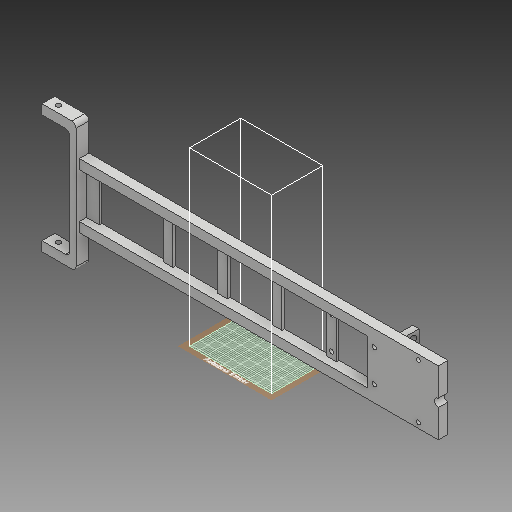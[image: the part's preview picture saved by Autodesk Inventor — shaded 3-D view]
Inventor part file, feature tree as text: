
AUTODESK INVENTOR PART (.ipt)
format: ipt  version: 2018 (Build 220112000, 112)  size: 794,624 bytes
history: native  units: mm
features: sketch x47, extrude x36, fillet x8, hole x6, plane x1
ambient origin geometry x8: Origin, YZ Plane, XZ Plane, XY Plane, X Axis, Y Axis, Z Axis, Center Point
bodies: Solid1 (feature_tree)
feature tree (98):
  extrude  "Extrusion1"  Depth=50.0mm
  hole  "Hole1"  [1 undecoded]
  hole  "Hole2"  [1 undecoded]
  extrude  "Extrusion2"  Depth=25.0mm
  extrude  "Extrusion3"  Depth=25.0mm
  extrude  "Extrusion4"  Depth=5.0mm
  sketch  "Sketch7"  dims[d25=10.0mm d26=5.0mm]
  extrude  "Extrusion5"  Depth=5.0mm
  extrude  "Extrusion6"  Depth=35.0mm
  extrude  "Extrusion7"  Depth=35.0mm
  extrude  "Extrusion8"  Depth=35.0mm
  extrude  "Extrusion9"  Depth=2.0mm TaperAngle=0.0deg
  extrude  "Extrusion10"  Depth=7.5mm TaperAngle=0.0deg
  extrude  "Extrusion11"  Depth=10.0mm
  extrude  "Extrusion12"  Depth=7.5mm
  fillet  "Fillet1"  Radius=7.5mm
  fillet  "Fillet2"  Radius=25.0mm
  fillet  "Fillet3"  Radius=3.0mm
  fillet  "Fillet4"  Radius=3.2mm
  fillet  "Fillet5"  Radius=2.1mm
  fillet  "Fillet6"  Radius=5.5mm
  extrude  "Extrusion13"  Depth=92.5mm TaperAngle=0.0deg
  sketch  "Sketch17"  dims[d58=4.25mm d59=241.0mm d60=0.0mm]
  hole  "Hole3"  [1 undecoded]
  hole  "Hole4"  [1 undecoded]
  extrude  "Extrusion14"  Depth=5.0mm
  extrude  "Extrusion15"  Depth=2.5mm TaperAngle=0.0deg
  extrude  "Extrusion16"  Depth=6.35mm
  extrude  "Extrusion17"  Depth=2.5mm
  extrude  "Extrusion18"  Depth=14.55mm TaperAngle=0.0deg
  extrude  "Extrusion19"  Depth=0.1mm
  extrude  "Extrusion20"  Depth=3.25mm
  extrude  "Extrusion21"  Depth=3.25mm
  hole  "Hole5"  [1 undecoded]
  extrude  "Extrusion22"  Depth=2.0mm
  extrude  "Extrusion23"  Depth=15.0mm
  extrude  "Extrusion24"  Depth=10.0mm TaperAngle=0.0deg
  hole  "Hole6"  [1 undecoded]
  extrude  "Extrusion25"  Depth=100.0mm TaperAngle=0.0deg
  extrude  "Extrusion26"  Depth=2.0mm TaperAngle=0.0deg
  sketch  "Sketch35"  dims[d116=3.3mm d117=3.3mm]
  plane  "Work Plane1"
  sketch  "Sketch36"  dims[d118=3.3mm d119=3.3mm d120=2.0mm d121=0.0mm]
  extrude  "Extrusion27"  Depth=3.3mm
  extrude  "Extrusion28"  Depth=2.0mm
  fillet  "Fillet7"  Radius=2.0mm
  extrude  "Extrusion29"  Depth=8.0mm
  extrude  "Extrusion30"  Depth=21.0mm
  extrude  "Extrusion31"  Depth=8.5mm
  extrude  "Extrusion32"  Depth=21.0mm
  sketch  "Sketch43"  dims[d142=10.0mm d143=0.0mm d144=7.5mm d145=0.0mm]
  fillet  "Fillet8"  Radius=3.3mm
  extrude  "Extrusion33"  Depth=3.3mm
  extrude  "Extrusion34"  Depth=7.5mm TaperAngle=0.0deg
  extrude  "Extrusion35"  Depth=15.0mm
  extrude  "Extrusion36"  Depth=100.0mm TaperAngle=0.0deg
  sketch  "Sketch1"  dims[d0=50.0mm d1=50.0mm]
  sketch  "Sketch2"  dims[d2=240.0mm d3=7.5mm]
  sketch  "Sketch3"  dims[d4=7.5mm d5=7.5mm d6=0.0mm]
  sketch  "Sketch4"  dims[d7=6.35mm d8=6.0mm d9=4.0mm d10=2.0mm d11=90.0deg d12=8.0mm d13=20.594885mm d14=25.0mm]
  sketch  "Sketch5"  dims[d15=3.3mm d16=6.0mm d17=4.0mm d18=2.0mm d19=90.0deg d20=8.0mm d21=20.594885mm d22=25.0mm]
  sketch  "Sketch6"  dims[d23=180.0deg d24=5.0mm]
  sketch  "Sketch8"  dims[d27=17.5mm d28=0.0mm d30=35.0mm]
  sketch  "Sketch9"  dims[d31=35.0mm d32=35.0mm]
  sketch  "Sketch10"  dims[d33=35.0mm d34=35.0mm]
  sketch  "Sketch11"  dims[d35=35.0mm d36=2.0mm d37=0.0mm]
  sketch  "Sketch12"  dims[d38=10.0mm d39=7.5mm d40=0.0mm]
  sketch  "Sketch13"  dims[d41=100.0mm d42=10.0mm]
  sketch  "Sketch14"  dims[d43=7.5mm d44=0.0mm d45=7.5mm d46=7.5mm d47=25.0mm d48=0.0mm d49=3.0mm d50=3.2mm d51=2.1mm d52=5.5mm]
  sketch  "Sketch15"  dims[d53=3.3mm d54=92.5mm d55=0.0mm]
  sketch  "Sketch16"  dims[d56=5.5mm d57=3.3mm]
  sketch  "Sketch18"  dims[d61=4.44mm d62=5.0mm]
  sketch  "Sketch19"  dims[d63=2.5mm d64=91.25mm d65=0.0mm]
  sketch  "Sketch20"  dims[d66=30.0mm d67=6.35mm]
  sketch  "Sketch21"  dims[d68=3.8mm d69=0.0mm d70=2.5mm]
  sketch  "Sketch22"  dims[d71=14.55mm d72=0.0mm d73=14.55mm d74=0.0mm]
  sketch  "Sketch23"  dims[d75=0.1mm d76=0.1mm]
  sketch  "Sketch24"  dims[d77=3.25mm d78=3.25mm]
  sketch  "Sketch25"  dims[d79=3.25mm d80=3.25mm]
  sketch  "Sketch26"  dims[d81=35.0mm d82=10.0mm]
  sketch  "Sketch27"  dims[d83=2.0mm d84=0.0mm d85=3.6mm]
  sketch  "Sketch28"  dims[d86=3.6mm]
  sketch  "Sketch29"  dims[d87=3.3mm d88=6.0mm d89=4.0mm d90=2.0mm d91=90.0deg d92=15.0mm d93=20.594885mm]
  sketch  "Sketch30"  dims[d94=3.3mm d95=6.0mm d96=4.0mm d97=2.0mm d98=90.0deg d99=15.0mm d100=20.594885mm d101=6.0mm]
  sketch  "Sketch31"  dims[d102=20.0mm d103=0.0mm d104=10.0mm d105=0.0mm]
  sketch  "Sketch32"  dims[d106=2.0mm d107=0.0mm d108=4.0mm]
  sketch  "Sketch33"  dims[d109=100.0mm d110=0.0mm d111=100.0mm d112=0.0mm]
  sketch  "Sketch34"  dims[d113=5.0mm d114=2.0mm d115=0.0mm]
  sketch  "Sketch37"  dims[d122=5.5mm d123=0.0mm]
  sketch  "Sketch38"  dims[d124=3.3mm d125=6.0mm d126=4.0mm d127=2.0mm d128=90.0deg d129=8.0mm d130=20.594885mm d131=42.0mm]
  sketch  "Sketch39"  dims[d132=17.0mm d133=21.0mm]
  sketch  "Sketch40"  dims[d135=8.5mm d136=15.825mm]
  sketch  "Sketch41"  dims[d137=3.5mm d138=21.0mm d139=3.3mm]
  sketch  "Sketch42"  dims[d140=3.3mm d141=3.3mm]
  sketch  "Sketch44"  dims[d146=100.0mm d147=0.0mm]
  sketch  "Sketch45"  dims[d148=5.0mm d149=6.0mm d150=4.0mm d151=2.0mm d152=90.0deg d153=15.0mm d154=0.0mm d155=3.75mm]
  sketch  "Sketch46"  dims[d156=100.0mm d157=0.0mm d158=100.0mm d159=0.0mm]
  sketch  "Sketch47"  dims[d160=-0.698132mm d161=5.0mm d162=5.0mm d163=37.5mm d164=0.0mm d165=1.1mm d166=37.5mm d167=0.0mm d168=0.2mm d169=3.0mm d170=5.5mm d171=0.0mm d172=10.0mm d173=0.0mm d174=74.724mm d175=74.724mm d176=85.515mm d177=5.0mm d178=85.515mm d179=5.0mm d180=85.515mm d181=5.0mm d182=85.515mm d183=5.0mm d184=2.0mm d185=0.0mm d186=10.0mm d187=2.0mm d188=0.0mm d189=2.0mm d190=1.0mm d191=0.0mm d192=2.0mm d193=0.0mm d194=10.0mm d195=1.0mm d196=0.0mm d197=20.0mm d198=1.0mm d199=0.0mm]
note: 6 required parameter values undecoded (feature->parameter linkage not recoverable at this tier; creation-order binding heuristic only, values carry confidence <= 0.55)
